# Revit family: P6343A75B,A2B
name_source: partatom
category: Plumbing Fixtures
revit_build: Autodesk Revit LT 2016 (Build: 20160525_1230(x64)
units: mm (PartAtom-declared; Revit-internal decimal feet)

## family parameters
Always vertical = Yes
Cut with Voids When Loaded = No
OmniClass Number = 23.45.05.14.17
OmniClass Title = Showers
Part Type = Normal
Room Calculation Point = No
Round Connector Dimension = Use Diameter
Shared = No
Work Plane-Based = No

## types (2) — shared parameters
Assembly Code = D2010700
Description = Shower Pan, Beveled Threshold
Keynote = 22 40 00.B3
Manufacturer = bestbath
Type Comments = ADA Compliant
URL = http://www.bestbath.com
Unit Depth = 44 1/4"
Unit Width = 62 1/2"

## per-type parameters (varying)
| type | Threshold Height | Unit Height |
| P6343A75B | 3/4" | 6" |
| P6343A2B | 2" | 7 1/4" |

note: column(s) folded — value = type name in every type: Model

## geometry (parser evidence)
native form markers: Blend x20, Sweep x2
no freeform markers — native parametric forms only
